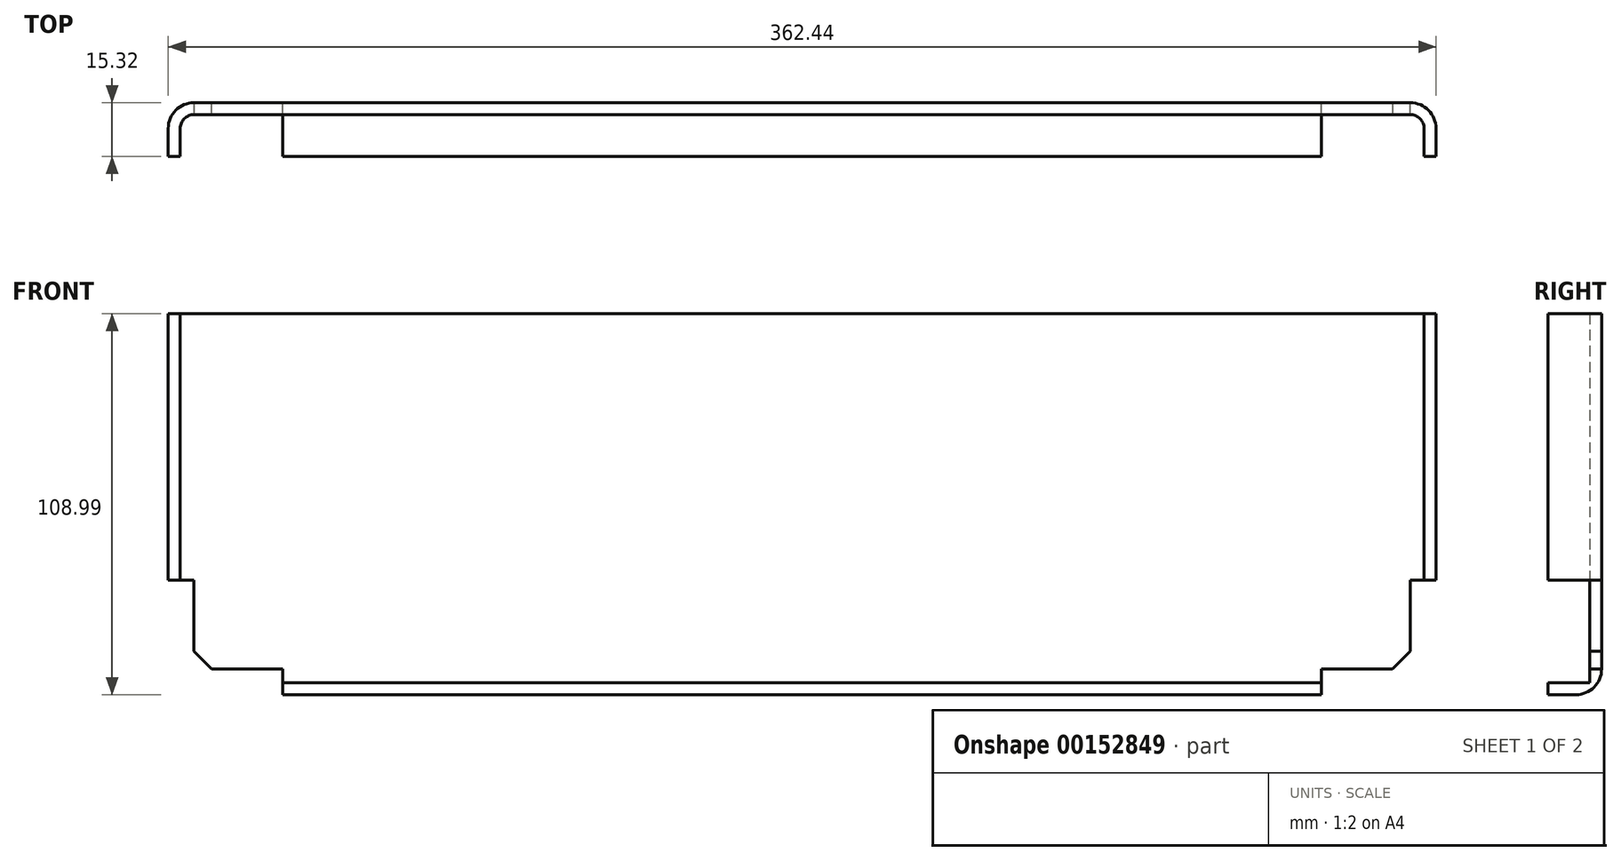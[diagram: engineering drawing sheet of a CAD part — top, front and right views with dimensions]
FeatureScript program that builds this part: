
annotation { "Feature Type Name" : "Feature", "Feature Type Description" : "" }
export const myFeature = defineFeature(function(context is Context, id is Id, definition is map)
    precondition{}
    {
        {
            var Q0;
            Q0=qCreatedBy(makeId("Top.planeOp"),FACE);
            var sketch = newSketch(context, id + "F0", { "sketchPlane" : qUnion([Q0])});
            skLineSegment(sketch, "E0.bottom", {"start": v(0, 0) * mm, "end": v(-3.42, 0) * mm});
            skLineSegment(sketch, "E1.left", {"start": v(0, 0) * mm, "end": v(0, 11.9) * mm});
            skLineSegment(sketch, "E1.right", {"start": v(-3.42, 0) * mm, "end": v(-3.42, 15.32) * mm});
            skLineSegment(sketch, "E2.bottom", {"start": v(0, 11.9) * mm, "end": v(355.6, 11.9) * mm});
            skLineSegment(sketch, "E2.top", {"start": v(-3.42, 15.32) * mm, "end": v(359.02, 15.32) * mm});
            skLineSegment(sketch, "E3", {"start": v(0, 11.9) * mm, "end": v(-3.42, 11.9) * mm, "construction": true});
            skLineSegment(sketch, "E4", {"start": v(0, 11.9) * mm, "end": v(0, 15.32) * mm, "construction": true});
            skLineSegment(sketch, "E5", {"start": v(355.6, 11.9) * mm, "end": v(355.6, 15.32) * mm, "construction": true});
            skLineSegment(sketch, "E6", {"start": v(355.6, 11.9) * mm, "end": v(359.02, 11.9) * mm, "construction": true});
            skLineSegment(sketch, "E7", {"start": v(359.02, 15.32) * mm, "end": v(359.02, 0) * mm});
            skLineSegment(sketch, "E8", {"start": v(359.02, 0) * mm, "end": v(355.6, 0) * mm});
            skLineSegment(sketch, "E9", {"start": v(355.6, 0) * mm, "end": v(355.6, 11.9) * mm});
            skSolve(sketch);
        }
        {
            var Q0;
            Q0=qSketchRegion(id+"F0",true);
            extrude(context, id + "F1", {"entities" : qUnion([Q0]), "depth" : 101.6 * mm});
        }
        {
            var Q0;
            Q0=makeQuery(id+"F1.opExtrude","SWEPT_FACE",FACE,{"disambiguationData":[OSD([sQuery(id+"F0.wireOp",EDGE,"E2.top")])]});
            var sketch = newSketch(context, id + "F2", { "sketchPlane" : qUnion([Q0])});
            skLineSegment(sketch, "E10.bottom", {"start": v(-3.97, 0) * mm, "end": v(-351.63, 0) * mm});
            skLineSegment(sketch, "E10.top", {"start": v(-3.97, -7.39) * mm, "end": v(-351.63, -7.39) * mm});
            skLineSegment(sketch, "E10.left", {"start": v(-3.97, 0) * mm, "end": v(-3.97, -7.39) * mm});
            skLineSegment(sketch, "E10.right", {"start": v(-351.63, 0) * mm, "end": v(-351.63, -7.39) * mm});
            skPoint(sketch, "E11", {"position": v(-177.8, 0) * mm});
            skSolve(sketch);
        }
        {
            var Q0;
            Q0=qSketchRegion(id+"F2",true);
            var Q1;
            Q1=makeQuery(id+"F1.opExtrude","SWEPT_FACE",FACE,{"disambiguationData":[OSD([sQuery(id+"F0.wireOp",EDGE,"E2.bottom")])]});
            extrude(context, id + "F3", {"entities" : qUnion([Q0]), "operationType" : NewBodyOperationType.ADD, "endBound" : BoundingType.UP_TO_SURFACE, "oppositeDirection" : true, "endBoundEntityFace" : qUnion([Q1]), "depth" : 25.4 * mm});
        }
        {
            var Q0;
            {var subQ0=sQuery(id+"F0.wireOp",EDGE,"E2.bottom");Q0=makeQuery(id+"F3.boolean.opBoolean","MERGE",FACE,{"derivedFrom":[makeQuery(id+"F1.opExtrude","SWEPT_FACE",FACE,{"disambiguationData":[OSD([subQ0])]}),makeQuery(id+"F3.opExtrude","CAP_FACE",FACE,{"disambiguationData":[OSD([subQ0]),ownerDisambiguation([makeQuery(id+"F3.opExtrude","SWEPT_BODY",BODY,{"disambiguationData":[OSD([sQuery(id+"F2.wireOp",EDGE,"E10.bottom"),sQuery(id+"F2.wireOp",EDGE,"E10.top"),sQuery(id+"F2.wireOp",EDGE,"E10.left"),sQuery(id+"F2.wireOp",EDGE,"E10.right")])]})])],"isStart":false}),makeQuery(id+"F3.opExtrude","CAP_FACE",FACE,{"disambiguationData":[OSD([subQ0]),ownerDisambiguation([makeQuery(id+"F3.opExtrude","SWEPT_BODY",BODY,{"disambiguationData":[OSD([sQuery(id+"F2.wireOp",EDGE,"UgydXLRX-frSp-zJC1-Wb66-JDDq08zRwpTB.bottom"),sQuery(id+"F2.wireOp",EDGE,"UgydXLRX-frSp-zJC1-Wb66-JDDq08zRwpTB.top"),sQuery(id+"F2.wireOp",EDGE,"UgydXLRX-frSp-zJC1-Wb66-JDDq08zRwpTB.left"),sQuery(id+"F2.wireOp",EDGE,"UgydXLRX-frSp-zJC1-Wb66-JDDq08zRwpTB.right")])]})])],"isStart":false})]});}
            var sketch = newSketch(context, id + "F4", { "sketchPlane" : qUnion([Q0])});
            skLineSegment(sketch, "E12.bottom", {"start": v(3.97, -7.39) * mm, "end": v(351.63, -7.39) * mm});
            skLineSegment(sketch, "E12.top", {"start": v(3.97, -3.97) * mm, "end": v(351.63, -3.97) * mm});
            skLineSegment(sketch, "E12.left", {"start": v(3.97, -7.39) * mm, "end": v(3.97, -3.97) * mm});
            skLineSegment(sketch, "E12.right", {"start": v(351.63, -7.39) * mm, "end": v(351.63, -3.97) * mm});
            skSolve(sketch);
        }
        {
            var Q0;
            Q0 = qSketchRegion(id + "F4", true);
            var Q1;
            Q1=makeQuery(id+"F1.opExtrude","SWEPT_FACE",FACE,{"disambiguationData":[OSD([sQuery(id+"F0.wireOp",EDGE,"E8")])]});
            extrude(context, id + "F5", {"entities" : qUnion([Q0]), "operationType" : NewBodyOperationType.ADD, "endBound" : BoundingType.UP_TO_SURFACE, "endBoundEntityFace" : qUnion([Q1]), "depth" : 25.4 * mm});
        }
        {
            var Q0;
            Q0=makeQuery(id+"F1.opExtrude","SWEPT_EDGE",EDGE,{"disambiguationData":[OSD([sQuery(id+"F0.wireOp",EDGE,"E1.left"),sQuery(id+"F0.wireOp",EDGE,"E2.bottom")])]});
            var Q1;
            Q1=makeQuery(id+"F1.opExtrude","SWEPT_EDGE",EDGE,{"disambiguationData":[OSD([sQuery(id+"F0.wireOp",EDGE,"E2.bottom"),sQuery(id+"F0.wireOp",EDGE,"E9")])]});
            var Q2;
            Q2=makeQuery(id+"F5.opExtrude","CAP_EDGE",EDGE,{"disambiguationData":[OSD([sQuery(id+"F4.wireOp",EDGE,"E12.top")])],"isStart":true});
            fillet(context, id + "F6", {"entities" : qUnion([Q0, Q1, Q2]), "radius" : 3.97 * mm, "tangentPropagation" : true, "allowEdgeOverflow" : false});
        }
        {
            var Q0;
            Q0=makeQuery(id+"F1.opExtrude","SWEPT_EDGE",EDGE,{"disambiguationData":[OSD([sQuery(id+"F0.wireOp",EDGE,"E1.right"),sQuery(id+"F0.wireOp",EDGE,"E2.top")])]});
            var Q1;
            Q1=makeQuery(id+"F3.opExtrude","CAP_EDGE",EDGE,{"disambiguationData":[OSD([sQuery(id+"F2.wireOp",EDGE,"UgydXLRX-frSp-zJC1-Wb66-JDDq08zRwpTB.top")])],"isStart":true});
            var Q2;
            Q2=makeQuery(id+"F1.opExtrude","SWEPT_EDGE",EDGE,{"disambiguationData":[OSD([sQuery(id+"F0.wireOp",EDGE,"E2.top"),sQuery(id+"F0.wireOp",EDGE,"E7")])]});
            var Q3;
            Q3=makeQuery(id+"F3.opExtrude","CAP_EDGE",EDGE,{"disambiguationData":[OSD([sQuery(id+"F2.wireOp",EDGE,"E10.top")])],"isStart":true});
            fillet(context, id + "F7", {"entities" : qUnion([Q0, Q1, Q2, Q3]), "radius" : 7.39 * mm, "tangentPropagation" : true, "allowEdgeOverflow" : false});
        }
        {
            var Q0;
            Q0=makeQuery(id+"F3.boolean.opBoolean","MERGE",FACE,{"derivedFrom":[makeQuery(id+"F1.opExtrude","SWEPT_FACE",FACE,{"disambiguationData":[OSD([sQuery(id+"F0.wireOp",EDGE,"E2.top")])]}),makeQuery(id+"F3.opExtrude","CAP_FACE",FACE,{"disambiguationData":[OSD([sQuery(id+"F2.wireOp",EDGE,"E10.bottom"),sQuery(id+"F2.wireOp",EDGE,"E10.top"),sQuery(id+"F2.wireOp",EDGE,"E10.left"),sQuery(id+"F2.wireOp",EDGE,"E10.right")])],"isStart":true}),makeQuery(id+"F3.opExtrude","CAP_FACE",FACE,{"disambiguationData":[OSD([sQuery(id+"F2.wireOp",EDGE,"UgydXLRX-frSp-zJC1-Wb66-JDDq08zRwpTB.bottom"),sQuery(id+"F2.wireOp",EDGE,"UgydXLRX-frSp-zJC1-Wb66-JDDq08zRwpTB.top"),sQuery(id+"F2.wireOp",EDGE,"UgydXLRX-frSp-zJC1-Wb66-JDDq08zRwpTB.left"),sQuery(id+"F2.wireOp",EDGE,"UgydXLRX-frSp-zJC1-Wb66-JDDq08zRwpTB.right")])],"isStart":true})]});
            var sketch = newSketch(context, id + "F8", { "sketchPlane" : qUnion([Q0])});
            skLineSegment(sketch, "E13.bottom", {"start": v(-351.63, 0) * mm, "end": v(-359.02, 0) * mm});
            skLineSegment(sketch, "E13.top", {"start": v(-351.63, 25.4) * mm, "end": v(-359.02, 25.4) * mm});
            skLineSegment(sketch, "E13.left", {"start": v(-351.63, 0) * mm, "end": v(-351.63, 25.4) * mm});
            skLineSegment(sketch, "E13.right", {"start": v(-359.02, 0) * mm, "end": v(-359.02, 25.4) * mm});
            skLineSegment(sketch, "E14.bottom", {"start": v(-351.63, 0) * mm, "end": v(-326.23, 0) * mm});
            skLineSegment(sketch, "E14.top", {"start": v(-351.63, -7.39) * mm, "end": v(-326.23, -7.39) * mm});
            skLineSegment(sketch, "E14.left", {"start": v(-351.63, 0) * mm, "end": v(-351.63, -7.39) * mm});
            skLineSegment(sketch, "E14.right", {"start": v(-326.23, 0) * mm, "end": v(-326.23, -7.39) * mm});
            skLineSegment(sketch, "E15.bottom", {"start": v(-3.97, 0) * mm, "end": v(3.42, 0) * mm});
            skLineSegment(sketch, "E15.top", {"start": v(-3.97, 25.4) * mm, "end": v(3.42, 25.4) * mm});
            skLineSegment(sketch, "E15.left", {"start": v(-3.97, 0) * mm, "end": v(-3.97, 25.4) * mm});
            skLineSegment(sketch, "E15.right", {"start": v(3.42, 0) * mm, "end": v(3.42, 25.4) * mm});
            skLineSegment(sketch, "E16.bottom", {"start": v(-3.97, 0) * mm, "end": v(-29.37, 0) * mm});
            skLineSegment(sketch, "E16.top", {"start": v(-3.97, -7.39) * mm, "end": v(-29.37, -7.39) * mm});
            skLineSegment(sketch, "E16.left", {"start": v(-3.97, 0) * mm, "end": v(-3.97, -7.39) * mm});
            skLineSegment(sketch, "E16.right", {"start": v(-29.37, 0) * mm, "end": v(-29.37, -7.39) * mm});
            skSolve(sketch);
        }
        {
            var Q0;
            Q0=qSketchRegion(id+"F8",true);
            var Q1;
            Q1=makeQuery(id+"F1.opExtrude","SWEPT_FACE",FACE,{"disambiguationData":[OSD([sQuery(id+"F0.wireOp",EDGE,"E0.bottom")])]});
            extrude(context, id + "F9", {"entities" : qUnion([Q0]), "operationType" : NewBodyOperationType.REMOVE, "endBound" : BoundingType.UP_TO_SURFACE, "oppositeDirection" : true, "endBoundEntityFace" : qUnion([Q1]), "depth" : 25.4 * mm});
        }
        {
            var Q0;
            {var subQ0=sQuery(id+"F8.wireOp",EDGE,"E13.left");var subQ1=sQuery(id+"F8.wireOp",EDGE,"E13.bottom");Q0=makeQuery(id+"F9.boolean.opBoolean","COPY",EDGE,{"derivedFrom":makeQuery(id+"F9.opExtrude","SWEPT_EDGE",EDGE,{"disambiguationData":[OSD([subQ1,subQ0,sQuery(id+"F8.wireOp",EDGE,"E14.bottom"),sQuery(id+"F8.wireOp",EDGE,"E14.left")]),ownerDisambiguation([makeQuery(id+"F9.opExtrude","SWEPT_BODY",BODY,{"disambiguationData":[OSD([subQ1,sQuery(id+"F8.wireOp",EDGE,"E13.top"),subQ0,sQuery(id+"F8.wireOp",EDGE,"E13.right")])]})])]})});}
            var Q1;
            {var subQ0=sQuery(id+"F8.wireOp",EDGE,"3Oe0S7Qs-8yx6-vlo6-Eu8V-P9BwxzaqcPTn.left");var subQ1=sQuery(id+"F8.wireOp",EDGE,"3Oe0S7Qs-8yx6-vlo6-Eu8V-P9BwxzaqcPTn.bottom");Q1=makeQuery(id+"F9.boolean.opBoolean","COPY",EDGE,{"derivedFrom":makeQuery(id+"F9.opExtrude","SWEPT_EDGE",EDGE,{"disambiguationData":[OSD([subQ1,subQ0,sQuery(id+"F8.wireOp",EDGE,"kPpFwlow-UMJp-mgX6-ve2c-XJOeRa5q08EM.bottom"),sQuery(id+"F8.wireOp",EDGE,"kPpFwlow-UMJp-mgX6-ve2c-XJOeRa5q08EM.left")]),ownerDisambiguation([makeQuery(id+"F9.opExtrude","SWEPT_BODY",BODY,{"disambiguationData":[OSD([subQ1,sQuery(id+"F8.wireOp",EDGE,"3Oe0S7Qs-8yx6-vlo6-Eu8V-P9BwxzaqcPTn.top"),subQ0,sQuery(id+"F8.wireOp",EDGE,"3Oe0S7Qs-8yx6-vlo6-Eu8V-P9BwxzaqcPTn.right")])]})])]})});}
            var Q2;
            {var subQ0=sQuery(id+"F8.wireOp",EDGE,"3Ok4dLKF-forT-Omcy-JCC2-O8Xur07eeOs5.left");var subQ1=sQuery(id+"F8.wireOp",EDGE,"3Ok4dLKF-forT-Omcy-JCC2-O8Xur07eeOs5.bottom");Q2=makeQuery(id+"F9.boolean.opBoolean","COPY",EDGE,{"derivedFrom":makeQuery(id+"F9.opExtrude","SWEPT_EDGE",EDGE,{"disambiguationData":[OSD([sQuery(id+"F8.wireOp",EDGE,"Th24o5HF-Wpam-jpX0-6mcy-5SkbfpQVNMsV.bottom"),sQuery(id+"F8.wireOp",EDGE,"Th24o5HF-Wpam-jpX0-6mcy-5SkbfpQVNMsV.left"),subQ1,subQ0]),ownerDisambiguation([makeQuery(id+"F9.opExtrude","SWEPT_BODY",BODY,{"disambiguationData":[OSD([subQ1,sQuery(id+"F8.wireOp",EDGE,"3Ok4dLKF-forT-Omcy-JCC2-O8Xur07eeOs5.top"),subQ0,sQuery(id+"F8.wireOp",EDGE,"3Ok4dLKF-forT-Omcy-JCC2-O8Xur07eeOs5.right")])]})])]})});}
            var Q3;
            {var subQ0=sQuery(id+"F8.wireOp",EDGE,"E15.left");var subQ1=sQuery(id+"F8.wireOp",EDGE,"E15.bottom");Q3=makeQuery(id+"F9.boolean.opBoolean","COPY",EDGE,{"derivedFrom":makeQuery(id+"F9.opExtrude","SWEPT_EDGE",EDGE,{"disambiguationData":[OSD([subQ1,subQ0,sQuery(id+"F8.wireOp",EDGE,"E16.bottom"),sQuery(id+"F8.wireOp",EDGE,"E16.left")]),ownerDisambiguation([makeQuery(id+"F9.opExtrude","SWEPT_BODY",BODY,{"disambiguationData":[OSD([subQ1,sQuery(id+"F8.wireOp",EDGE,"E15.top"),subQ0,sQuery(id+"F8.wireOp",EDGE,"E15.right")])]})])]})});}
            chamfer(context, id + "F10", {"entities" : qUnion([Q0, Q1, Q2, Q3]), "width" : 5.08 * mm, "tangentPropagation" : true});
        }
    });
